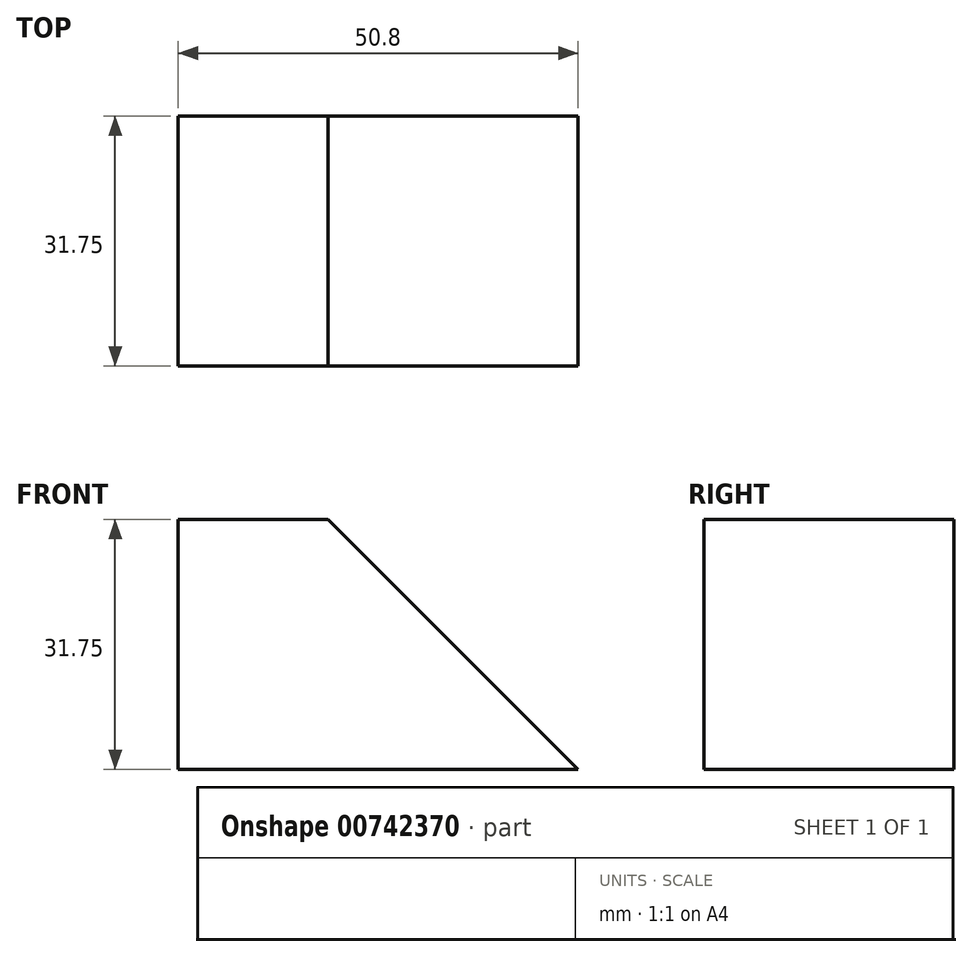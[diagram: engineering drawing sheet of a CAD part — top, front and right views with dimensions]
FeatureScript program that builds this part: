
annotation { "Feature Type Name" : "Feature", "Feature Type Description" : "" }
export const myFeature = defineFeature(function(context is Context, id is Id, definition is map)
    precondition{}
    {
        {
            var Q0;
            Q0=qCreatedBy(makeId("Front.planeOp"),FACE);
            var sketch = newSketch(context, id + "F0", { "sketchPlane" : qUnion([Q0])});
            skLineSegment(sketch, "E0.bottom", {"start": v(0, 0) * mm, "end": v(-50.8, 0) * mm});
            skLineSegment(sketch, "E0.top", {"start": v(0, 31.75) * mm, "end": v(-50.8, 31.75) * mm});
            skLineSegment(sketch, "E0.left", {"start": v(0, 0) * mm, "end": v(0, 31.75) * mm});
            skLineSegment(sketch, "E0.right", {"start": v(-50.8, 0) * mm, "end": v(-50.8, 31.75) * mm});
            skSolve(sketch);
        }
        {
            var Q0;
            Q0 = qSketchRegion(id + "F0", true);
            extrude(context, id + "F1", {"entities" : qUnion([Q0]), "depth" : 31.75 * mm, "offsetDistance" : 25.4 * mm});
        }
        {
            var Q0;
            Q0=makeQuery(id+"F1.opExtrude","CAP_FACE",FACE,{"disambiguationData":[OSD([sQuery(id+"F0.wireOp",EDGE,"E0.bottom"),sQuery(id+"F0.wireOp",EDGE,"E0.top"),sQuery(id+"F0.wireOp",EDGE,"E0.left"),sQuery(id+"F0.wireOp",EDGE,"E0.right")])],"isStart":false});
            var sketch = newSketch(context, id + "F2", { "sketchPlane" : qUnion([Q0])});
            skLineSegment(sketch, "E1", {"start": v(-31.75, 31.75) * mm, "end": v(0, 0) * mm});
            skSolve(sketch);
        }
        {
            var Q0;
            {var subQ0=sQuery(id+"F2.wireOp",EDGE,"E1");Q0=makeQuery(id+"F2.imprint","IMPRINT",FACE,{"disambiguationData":[TD([[makeQuery(id+"F2.imprint","IMPRINT",EDGE,{"derivedFrom":subQ0}),1.0]])]});}
            extrude(context, id + "F3", {"entities" : qUnion([Q0]), "operationType" : NewBodyOperationType.REMOVE, "endBound" : BoundingType.THROUGH_ALL, "oppositeDirection" : true, "depth" : 25.4 * mm, "offsetDistance" : 25.4 * mm});
        }
        {
            var Q0;
            Q0=makeQuery(id+"F3.boolean.opBoolean","COPY",FACE,{"derivedFrom":makeQuery(id+"F3.opExtrude","SWEPT_FACE",FACE,{"disambiguationData":[OSD([sQuery(id+"F2.wireOp",EDGE,"E1")])]})});
            var sketch = newSketch(context, id + "F4", { "sketchPlane" : qUnion([Q0])});
            skLineSegment(sketch, "E2.bottom", {"start": v(0, 0) * mm, "end": v(-19.05, 0) * mm});
            skLineSegment(sketch, "E2.top", {"start": v(0, -19.05) * mm, "end": v(-19.05, -19.05) * mm});
            skLineSegment(sketch, "E2.left", {"start": v(0, 0) * mm, "end": v(0, -19.05) * mm});
            skLineSegment(sketch, "E2.right", {"start": v(-19.05, 0) * mm, "end": v(-19.05, -19.05) * mm});
            skSolve(sketch);
        }
        {
            var Q0;
            Q0=makeQuery(id+"F4.imprint","IMPRINT",FACE,{"disambiguationData":[TD([[makeQuery(id+"F4.imprint","IMPRINT",EDGE,{"derivedFrom":sQuery(id+"F4.wireOp",EDGE,"E2.bottom")}),-1.0]])]});
            extrude(context, id + "F5", {"entities" : qUnion([Q0]), "operationType" : NewBodyOperationType.ADD, "depth" : 19.05 * mm, "offsetDistance" : 25.4 * mm});
        }
        {
            var Q0;
            Q0=makeQuery(id+"F5.opExtrude","SWEPT_FACE",FACE,{"disambiguationData":[OSD([sQuery(id+"F4.wireOp",EDGE,"E2.top")])]});
            var sketch = newSketch(context, id + "F6", { "sketchPlane" : qUnion([Q0])});
            skLineSegment(sketch, "E3", {"start": v(0, 0) * mm, "end": v(0, 13.72) * mm});
            skLineSegment(sketch, "E4", {"start": v(0, 13.72) * mm, "end": v(-13.47, 13.47) * mm});
            skSolve(sketch);
        }
        {
            var Q0;
            Q0=makeQuery(id+"F6.imprint","IMPRINT",FACE,{"disambiguationData":[TD([[makeQuery(id+"F6.imprint","IMPRINT",EDGE,{"derivedFrom":sQuery(id+"F6.wireOp",EDGE,"E3")}),-1.0]])]});
            extrude(context, id + "F7", {"entities" : qUnion([Q0]), "operationType" : NewBodyOperationType.REMOVE, "endBound" : BoundingType.THROUGH_ALL, "oppositeDirection" : true, "depth" : 25.4 * mm, "offsetDistance" : 25.4 * mm});
        }
    });
